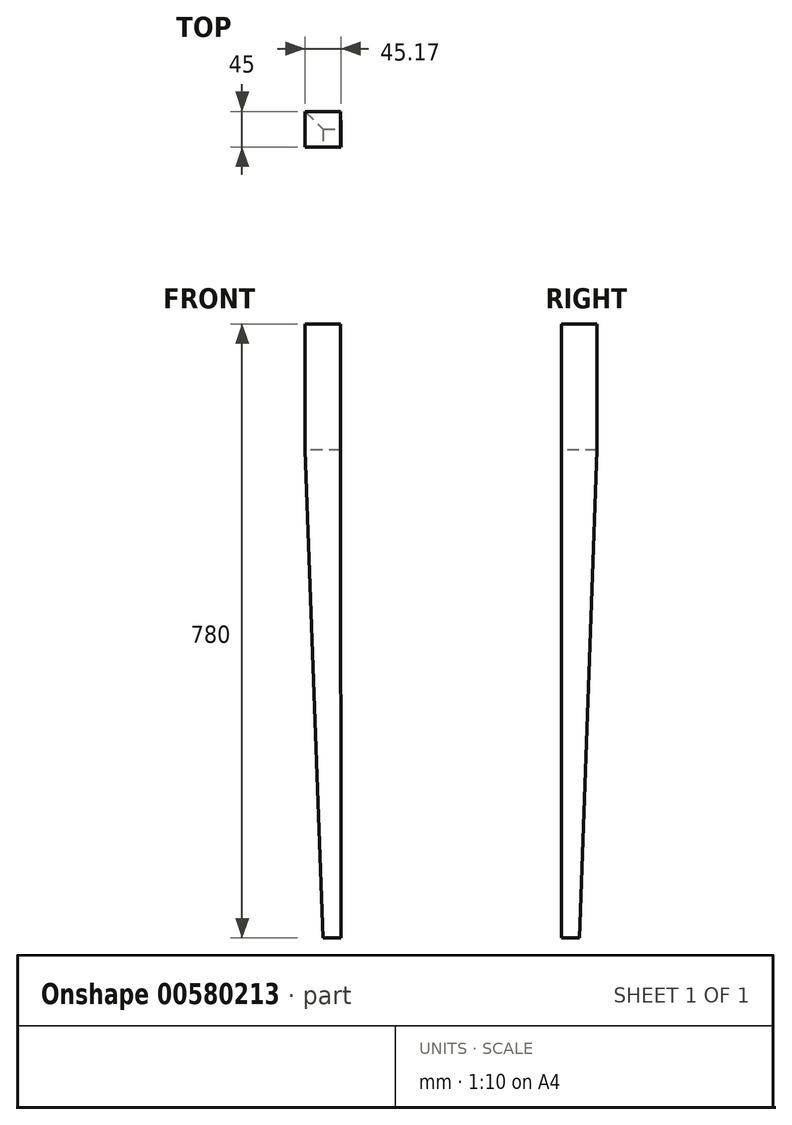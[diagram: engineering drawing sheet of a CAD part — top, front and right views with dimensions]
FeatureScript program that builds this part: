
annotation { "Feature Type Name" : "Feature", "Feature Type Description" : "" }
export const myFeature = defineFeature(function(context is Context, id is Id, definition is map)
    precondition{}
    {
        {
            var Q0;
            Q0=qCreatedBy(makeId("Top.planeOp"),FACE);
            var sketch = newSketch(context, id + "F0", { "sketchPlane" : qUnion([Q0])});
            skLineSegment(sketch, "E0.bottom", {"start": v(22.5, 22.5) * mm, "end": v(-22.5, 22.5) * mm});
            skLineSegment(sketch, "E0.top", {"start": v(22.5, -22.5) * mm, "end": v(-22.5, -22.5) * mm});
            skLineSegment(sketch, "E0.left", {"start": v(22.5, 22.5) * mm, "end": v(22.5, -22.5) * mm});
            skLineSegment(sketch, "E0.right", {"start": v(-22.5, 22.5) * mm, "end": v(-22.5, -22.5) * mm});
            skPoint(sketch, "E0.middle", {"position": v(0, 0) * mm});
            skSolve(sketch);
        }
        {
            var Q0;
            Q0=qCreatedBy(makeId("Top.planeOp"),FACE);
            cPlane(context, id + "F1", {"entities" : qUnion([Q0]), "cplaneType" : CPlaneType.OFFSET, "offset" : 620 * mm, "oppositeDirection" : true, "width" : 150 * mm, "height" : 150 * mm});
        }
        {
            var Q0;
            Q0=qCreatedBy(id+"F1.planeOp",FACE);
            var sketch = newSketch(context, id + "F2", { "sketchPlane" : qUnion([Q0])});
            skLineSegment(sketch, "E1.bottom", {"start": v(0, 0) * mm, "end": v(22.67, 0) * mm});
            skLineSegment(sketch, "E1.top", {"start": v(0, -22.5) * mm, "end": v(22.67, -22.5) * mm});
            skLineSegment(sketch, "E1.left", {"start": v(0, 0) * mm, "end": v(0, -22.5) * mm});
            skLineSegment(sketch, "E1.right", {"start": v(22.67, 0) * mm, "end": v(22.67, -22.5) * mm});
            skSolve(sketch);
        }
        {
            var Q0;
            Q0=makeQuery(id+"F0.imprint","IMPRINT",FACE,{"disambiguationData":[TD([[makeQuery(id+"F0.imprint","IMPRINT",EDGE,{"derivedFrom":sQuery(id+"F0.wireOp",EDGE,"E0.bottom")}),1.0]])]});
            var Q1;
            Q1=makeQuery(id+"F2.imprint","IMPRINT",FACE,{"disambiguationData":[TD([[makeQuery(id+"F2.imprint","IMPRINT",EDGE,{"derivedFrom":sQuery(id+"F2.wireOp",EDGE,"E1.bottom")}),-1.0]])]});
            loft(context, id + "F3", {"sheetProfilesArray" : [{ "sheetProfileEntities" : qUnion([Q0]) }, { "sheetProfileEntities" : qUnion([Q1]) }]});
        }
        {
            var Q0;
            Q0=makeQuery(id+"F0.imprint","IMPRINT",FACE,{"disambiguationData":[TD([[makeQuery(id+"F0.imprint","IMPRINT",EDGE,{"derivedFrom":sQuery(id+"F0.wireOp",EDGE,"E0.bottom")}),1.0]])]});
            extrude(context, id + "F4", {"entities" : qUnion([Q0]), "operationType" : NewBodyOperationType.ADD, "depth" : 160 * mm, "offsetDistance" : 25 * mm});
        }
    });
